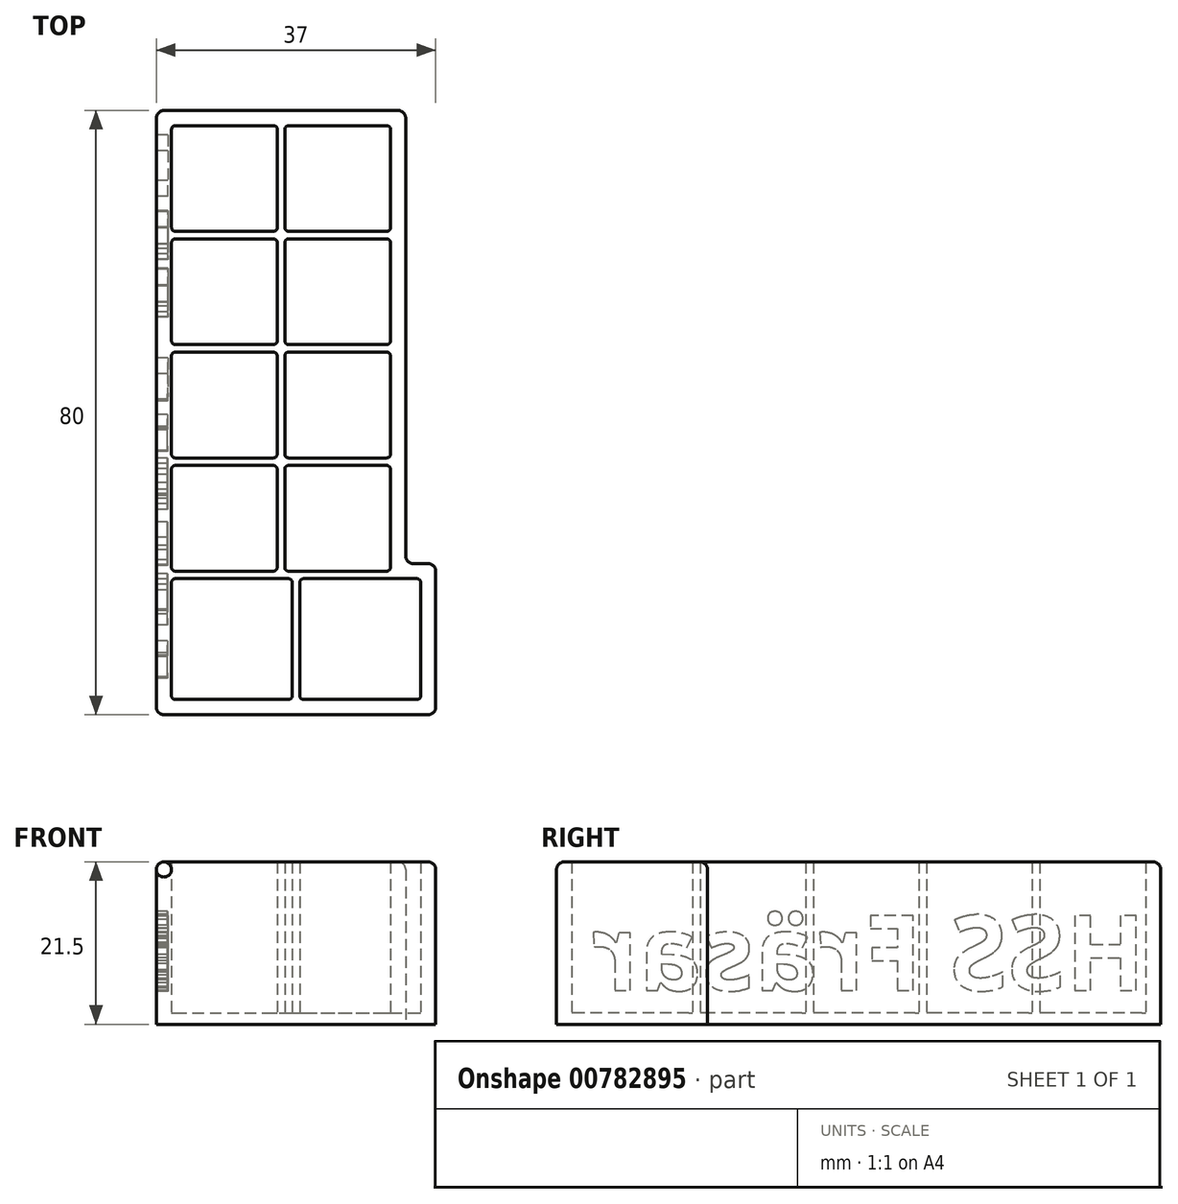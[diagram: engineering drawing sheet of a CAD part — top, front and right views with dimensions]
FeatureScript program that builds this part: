
annotation { "Feature Type Name" : "Feature", "Feature Type Description" : "" }
export const myFeature = defineFeature(function(context is Context, id is Id, definition is map)
    precondition{}
    {
        {
            var Q0;
            Q0=qCreatedBy(makeId("Top.planeOp"),FACE);
            var sketch = newSketch(context, id + "F0", { "sketchPlane" : qUnion([Q0])});
            skLineSegment(sketch, "E0.bottom", {"start": v(-10.2, 14) * mm, "end": v(3.8, 14) * mm});
            skLineSegment(sketch, "E0.top", {"start": v(-10.2, 0) * mm, "end": v(3.8, 0) * mm});
            skLineSegment(sketch, "E0.left", {"start": v(-10.2, 14) * mm, "end": v(-10.2, 0) * mm});
            skLineSegment(sketch, "E0.right", {"start": v(3.8, 14) * mm, "end": v(3.8, 0) * mm});
            skLineSegment(sketch, "E1.0.1.0", {"start": v(-10.2, -1) * mm, "end": v(3.8, -1) * mm});
            skLineSegment(sketch, "E1.0.1.1", {"start": v(-10.2, -1) * mm, "end": v(-10.2, -15) * mm});
            skLineSegment(sketch, "E1.0.1.2", {"start": v(3.8, -1) * mm, "end": v(3.8, -15) * mm});
            skLineSegment(sketch, "E1.0.1.3", {"start": v(-10.2, -15) * mm, "end": v(3.8, -15) * mm});
            skLineSegment(sketch, "E1.0.2.0", {"start": v(-10.2, -16) * mm, "end": v(3.8, -16) * mm});
            skLineSegment(sketch, "E1.0.2.1", {"start": v(-10.2, -16) * mm, "end": v(-10.2, -30) * mm});
            skLineSegment(sketch, "E1.0.2.2", {"start": v(3.8, -16) * mm, "end": v(3.8, -30) * mm});
            skLineSegment(sketch, "E1.0.2.3", {"start": v(-10.2, -30) * mm, "end": v(3.8, -30) * mm});
            skLineSegment(sketch, "E1.0.3.0", {"start": v(-10.2, -31) * mm, "end": v(3.8, -31) * mm});
            skLineSegment(sketch, "E1.0.3.1", {"start": v(-10.2, -31) * mm, "end": v(-10.2, -45) * mm});
            skLineSegment(sketch, "E1.0.3.2", {"start": v(3.8, -31) * mm, "end": v(3.8, -45) * mm});
            skLineSegment(sketch, "E1.0.3.3", {"start": v(-10.2, -45) * mm, "end": v(3.8, -45) * mm});
            skLineSegment(sketch, "E1.1.0.0", {"start": v(4.8, 14) * mm, "end": v(18.8, 14) * mm});
            skLineSegment(sketch, "E1.1.0.1", {"start": v(4.8, 14) * mm, "end": v(4.8, 0) * mm});
            skLineSegment(sketch, "E1.1.0.2", {"start": v(18.8, 14) * mm, "end": v(18.8, 0) * mm});
            skLineSegment(sketch, "E1.1.0.3", {"start": v(4.8, 0) * mm, "end": v(18.8, 0) * mm});
            skLineSegment(sketch, "E1.1.1.0", {"start": v(4.8, -1) * mm, "end": v(18.8, -1) * mm});
            skLineSegment(sketch, "E1.1.1.1", {"start": v(4.8, -1) * mm, "end": v(4.8, -15) * mm});
            skLineSegment(sketch, "E1.1.1.2", {"start": v(18.8, -1) * mm, "end": v(18.8, -15) * mm});
            skLineSegment(sketch, "E1.1.1.3", {"start": v(4.8, -15) * mm, "end": v(18.8, -15) * mm});
            skLineSegment(sketch, "E1.1.2.0", {"start": v(4.8, -16) * mm, "end": v(18.8, -16) * mm});
            skLineSegment(sketch, "E1.1.2.1", {"start": v(4.8, -16) * mm, "end": v(4.8, -30) * mm});
            skLineSegment(sketch, "E1.1.2.2", {"start": v(18.8, -16) * mm, "end": v(18.8, -30) * mm});
            skLineSegment(sketch, "E1.1.2.3", {"start": v(4.8, -30) * mm, "end": v(18.8, -30) * mm});
            skLineSegment(sketch, "E1.1.3.0", {"start": v(4.8, -31) * mm, "end": v(18.8, -31) * mm});
            skLineSegment(sketch, "E1.1.3.1", {"start": v(4.8, -31) * mm, "end": v(4.8, -45) * mm});
            skLineSegment(sketch, "E1.1.3.2", {"start": v(18.8, -31) * mm, "end": v(18.8, -45) * mm});
            skLineSegment(sketch, "E1.1.3.3", {"start": v(4.8, -45) * mm, "end": v(18.8, -45) * mm});
            skLineSegment(sketch, "E1.direction1", {"start": v(-10.2, 14) * mm, "end": v(4.8, 14) * mm, "construction": true});
            skLineSegment(sketch, "E1.direction2", {"start": v(-10.2, 14) * mm, "end": v(-10.2, -1) * mm, "construction": true});
            skLineSegment(sketch, "E2.bottom", {"start": v(-10.2, -46) * mm, "end": v(5.8, -46) * mm});
            skLineSegment(sketch, "E2.top", {"start": v(-10.2, -62) * mm, "end": v(5.8, -62) * mm});
            skLineSegment(sketch, "E2.left", {"start": v(-10.2, -46) * mm, "end": v(-10.2, -62) * mm});
            skLineSegment(sketch, "E2.right", {"start": v(5.8, -46) * mm, "end": v(5.8, -62) * mm});
            skLineSegment(sketch, "E3.1.0.0", {"start": v(22.8, -46) * mm, "end": v(22.8, -62) * mm});
            skLineSegment(sketch, "E3.1.0.1", {"start": v(6.8, -46) * mm, "end": v(22.8, -46) * mm});
            skLineSegment(sketch, "E3.1.0.2", {"start": v(6.8, -46) * mm, "end": v(6.8, -62) * mm});
            skLineSegment(sketch, "E3.1.0.3", {"start": v(6.8, -62) * mm, "end": v(22.8, -62) * mm});
            skLineSegment(sketch, "E3.direction1", {"start": v(5.8, -62) * mm, "end": v(22.8, -62) * mm, "construction": true});
            skSolve(sketch);
        }
        {
            var Q0;
            Q0=qCreatedBy(makeId("Top.planeOp"),FACE);
            var sketch = newSketch(context, id + "F1", { "sketchPlane" : qUnion([Q0])});
            skLineSegment(sketch, "E4", {"start": v(-10.2, 14) * mm, "end": v(18.8, 14) * mm});
            skLineSegment(sketch, "E5", {"start": v(18.8, 14) * mm, "end": v(18.8, -46) * mm});
            skLineSegment(sketch, "E6", {"start": v(18.8, -46) * mm, "end": v(22.8, -46) * mm});
            skLineSegment(sketch, "E7", {"start": v(22.8, -46) * mm, "end": v(22.8, -62) * mm});
            skLineSegment(sketch, "E8", {"start": v(22.8, -62) * mm, "end": v(-10.2, -62) * mm});
            skLineSegment(sketch, "E9", {"start": v(-10.2, -62) * mm, "end": v(-10.2, 14) * mm});
            skLineSegment(sketch, "E10.0", {"start": v(20.8, 16) * mm, "end": v(20.8, -44) * mm});
            skLineSegment(sketch, "E10.1", {"start": v(24.8, -44) * mm, "end": v(24.8, -64) * mm});
            skLineSegment(sketch, "E10.2", {"start": v(24.8, -64) * mm, "end": v(-12.21, -64) * mm});
            skLineSegment(sketch, "E10.3", {"start": v(20.8, -44) * mm, "end": v(24.8, -44) * mm});
            skLineSegment(sketch, "E10.4", {"start": v(-12.21, -64) * mm, "end": v(-12.2, 16) * mm});
            skLineSegment(sketch, "E10.5", {"start": v(-12.2, 16) * mm, "end": v(20.8, 16) * mm});
            skSolve(sketch);
        }
        {
            var Q0;
            Q0=makeQuery(id+"F1.imprint","IMPRINT",FACE,{"disambiguationData":[TD([[makeQuery(id+"F1.imprint","IMPRINT",EDGE,{"derivedFrom":sQuery(id+"F1.wireOp",EDGE,"E4")}),1.0]])]});
            var Q1;
            Q1=makeQuery(id+"F1.imprint","IMPRINT",FACE,{"disambiguationData":[TD([[makeQuery(id+"F1.imprint","IMPRINT",EDGE,{"derivedFrom":sQuery(id+"F1.wireOp",EDGE,"E4")}),-1.0]])]});
            extrude(context, id + "F2", {"entities" : qUnion([Q0, Q1]), "depth" : 20 * mm, "offsetDistance" : 25 * mm, "hasSecondDirection" : true, "secondDirectionOppositeDirection" : true, "secondDirectionDepth" : 1.5 * mm});
        }
        {
            var Q0;
            Q0=makeQuery(id+"F0.imprint","IMPRINT",FACE,{"disambiguationData":[TD([[makeQuery(id+"F0.imprint","IMPRINT",EDGE,{"derivedFrom":sQuery(id+"F0.wireOp",EDGE,"E0.bottom")}),-1.0]])]});
            var Q1;
            Q1=makeQuery(id+"F0.imprint","IMPRINT",FACE,{"disambiguationData":[TD([[makeQuery(id+"F0.imprint","IMPRINT",EDGE,{"derivedFrom":sQuery(id+"F0.wireOp",EDGE,"E1.1.0.0")}),-1.0]])]});
            var Q2;
            Q2=makeQuery(id+"F0.imprint","IMPRINT",FACE,{"disambiguationData":[TD([[makeQuery(id+"F0.imprint","IMPRINT",EDGE,{"derivedFrom":sQuery(id+"F0.wireOp",EDGE,"E1.0.1.0")}),-1.0]])]});
            var Q3;
            Q3=makeQuery(id+"F0.imprint","IMPRINT",FACE,{"disambiguationData":[TD([[makeQuery(id+"F0.imprint","IMPRINT",EDGE,{"derivedFrom":sQuery(id+"F0.wireOp",EDGE,"E1.1.1.0")}),-1.0]])]});
            var Q4;
            Q4=makeQuery(id+"F0.imprint","IMPRINT",FACE,{"disambiguationData":[TD([[makeQuery(id+"F0.imprint","IMPRINT",EDGE,{"derivedFrom":sQuery(id+"F0.wireOp",EDGE,"E1.0.2.0")}),-1.0]])]});
            var Q5;
            Q5=makeQuery(id+"F0.imprint","IMPRINT",FACE,{"disambiguationData":[TD([[makeQuery(id+"F0.imprint","IMPRINT",EDGE,{"derivedFrom":sQuery(id+"F0.wireOp",EDGE,"E1.1.2.0")}),-1.0]])]});
            var Q6;
            Q6=makeQuery(id+"F0.imprint","IMPRINT",FACE,{"disambiguationData":[TD([[makeQuery(id+"F0.imprint","IMPRINT",EDGE,{"derivedFrom":sQuery(id+"F0.wireOp",EDGE,"E1.0.3.0")}),-1.0]])]});
            var Q7;
            Q7=makeQuery(id+"F0.imprint","IMPRINT",FACE,{"disambiguationData":[TD([[makeQuery(id+"F0.imprint","IMPRINT",EDGE,{"derivedFrom":sQuery(id+"F0.wireOp",EDGE,"E1.1.3.0")}),-1.0]])]});
            var Q8;
            Q8=makeQuery(id+"F0.imprint","IMPRINT",FACE,{"disambiguationData":[TD([[makeQuery(id+"F0.imprint","IMPRINT",EDGE,{"derivedFrom":sQuery(id+"F0.wireOp",EDGE,"E2.bottom")}),-1.0]])]});
            var Q9;
            Q9=makeQuery(id+"F0.imprint","IMPRINT",FACE,{"disambiguationData":[TD([[makeQuery(id+"F0.imprint","IMPRINT",EDGE,{"derivedFrom":sQuery(id+"F0.wireOp",EDGE,"E3.1.0.0")}),-1.0]])]});
            var Q10;
            Q10=makeQuery(id+"F2.opExtrude","CAP_FACE",FACE,{"disambiguationData":[OSD([sQuery(id+"F1.wireOp",EDGE,"E10.0"),sQuery(id+"F1.wireOp",EDGE,"E10.1"),sQuery(id+"F1.wireOp",EDGE,"E10.2"),sQuery(id+"F1.wireOp",EDGE,"E10.3"),sQuery(id+"F1.wireOp",EDGE,"E10.4"),sQuery(id+"F1.wireOp",EDGE,"E10.5")])],"isStart":false});
            extrude(context, id + "F3", {"entities" : qUnion([Q0, Q1, Q2, Q3, Q4, Q5, Q6, Q7, Q8, Q9]), "operationType" : NewBodyOperationType.REMOVE, "endBound" : BoundingType.UP_TO_SURFACE, "depth" : 25 * mm, "endBoundEntityFace" : qUnion([Q10]), "offsetDistance" : 25 * mm});
        }
        {
            var Q0;
            Q0=makeQuery(id+"F2.opExtrude","CAP_EDGE",EDGE,{"disambiguationData":[OSD([sQuery(id+"F1.wireOp",EDGE,"E10.0")])],"isStart":false});
            var Q1;
            Q1=makeQuery(id+"F2.opExtrude","CAP_EDGE",EDGE,{"disambiguationData":[OSD([sQuery(id+"F1.wireOp",EDGE,"E10.3")])],"isStart":false});
            var Q2;
            Q2=makeQuery(id+"F2.opExtrude","CAP_EDGE",EDGE,{"disambiguationData":[OSD([sQuery(id+"F1.wireOp",EDGE,"E10.1")])],"isStart":false});
            var Q3;
            Q3=makeQuery(id+"F2.opExtrude","CAP_EDGE",EDGE,{"disambiguationData":[OSD([sQuery(id+"F1.wireOp",EDGE,"E10.4")])],"isStart":false});
            var Q4;
            Q4=makeQuery(id+"F2.opExtrude","SWEPT_EDGE",EDGE,{"disambiguationData":[OSD([sQuery(id+"F1.wireOp",EDGE,"E10.1"),sQuery(id+"F1.wireOp",EDGE,"E10.2")])]});
            var Q5;
            Q5=makeQuery(id+"F2.opExtrude","SWEPT_EDGE",EDGE,{"disambiguationData":[OSD([sQuery(id+"F1.wireOp",EDGE,"E10.1"),sQuery(id+"F1.wireOp",EDGE,"E10.3")])]});
            var Q6;
            Q6=makeQuery(id+"F2.opExtrude","SWEPT_EDGE",EDGE,{"disambiguationData":[OSD([sQuery(id+"F1.wireOp",EDGE,"E10.0"),sQuery(id+"F1.wireOp",EDGE,"E10.5")])]});
            var Q7;
            Q7=makeQuery(id+"F2.opExtrude","CAP_EDGE",EDGE,{"disambiguationData":[OSD([sQuery(id+"F1.wireOp",EDGE,"E10.5")])],"isStart":false});
            var Q8;
            Q8=makeQuery(id+"F2.opExtrude","SWEPT_EDGE",EDGE,{"disambiguationData":[OSD([sQuery(id+"F1.wireOp",EDGE,"E10.4"),sQuery(id+"F1.wireOp",EDGE,"E10.5")])]});
            var Q9;
            Q9=makeQuery(id+"F2.opExtrude","SWEPT_EDGE",EDGE,{"disambiguationData":[OSD([sQuery(id+"F1.wireOp",EDGE,"E10.0"),sQuery(id+"F1.wireOp",EDGE,"E10.3")])]});
            var Q10;
            Q10=makeQuery(id+"F2.opExtrude","CAP_EDGE",EDGE,{"disambiguationData":[OSD([sQuery(id+"F1.wireOp",EDGE,"E10.2")])],"isStart":false});
            var Q11;
            Q11=makeQuery(id+"F2.opExtrude","SWEPT_EDGE",EDGE,{"disambiguationData":[OSD([sQuery(id+"F1.wireOp",EDGE,"E10.2"),sQuery(id+"F1.wireOp",EDGE,"E10.4")])]});
            fillet(context, id + "F4", {"entities" : qUnion([Q0, Q1, Q2, Q3, Q4, Q5, Q6, Q7, Q8, Q9, Q10, Q11]), "radius" : 1 * mm, "allowEdgeOverflow" : false});
        }
        {
            var Q0;
            Q0=makeQuery(id+"F3.boolean.opBoolean","COPY",EDGE,{"derivedFrom":makeQuery(id+"F3.opExtrude","SWEPT_EDGE",EDGE,{"disambiguationData":[OSD([sQuery(id+"F0.wireOp",EDGE,"E1.1.0.0"),sQuery(id+"F0.wireOp",EDGE,"E1.1.0.2")])]})});
            var Q1;
            Q1=makeQuery(id+"F3.boolean.opBoolean","COPY",EDGE,{"derivedFrom":makeQuery(id+"F3.opExtrude","SWEPT_EDGE",EDGE,{"disambiguationData":[OSD([sQuery(id+"F0.wireOp",EDGE,"E1.1.1.0"),sQuery(id+"F0.wireOp",EDGE,"E1.1.1.2")])]})});
            var Q2;
            Q2=makeQuery(id+"F3.boolean.opBoolean","COPY",EDGE,{"derivedFrom":makeQuery(id+"F3.opExtrude","SWEPT_EDGE",EDGE,{"disambiguationData":[OSD([sQuery(id+"F0.wireOp",EDGE,"E1.1.2.0"),sQuery(id+"F0.wireOp",EDGE,"E1.1.2.2")])]})});
            var Q3;
            Q3=makeQuery(id+"F3.boolean.opBoolean","COPY",EDGE,{"derivedFrom":makeQuery(id+"F3.opExtrude","SWEPT_EDGE",EDGE,{"disambiguationData":[OSD([sQuery(id+"F0.wireOp",EDGE,"E1.1.3.0"),sQuery(id+"F0.wireOp",EDGE,"E1.1.3.2")])]})});
            var Q4;
            Q4=makeQuery(id+"F3.boolean.opBoolean","COPY",EDGE,{"derivedFrom":makeQuery(id+"F3.opExtrude","SWEPT_EDGE",EDGE,{"disambiguationData":[OSD([sQuery(id+"F0.wireOp",EDGE,"E3.1.0.0"),sQuery(id+"F0.wireOp",EDGE,"E3.1.0.1")])]})});
            var Q5;
            Q5=makeQuery(id+"F3.boolean.opBoolean","COPY",EDGE,{"derivedFrom":makeQuery(id+"F3.opExtrude","SWEPT_EDGE",EDGE,{"disambiguationData":[OSD([sQuery(id+"F0.wireOp",EDGE,"E0.bottom"),sQuery(id+"F0.wireOp",EDGE,"E0.right")])]})});
            var Q6;
            Q6=makeQuery(id+"F3.boolean.opBoolean","COPY",EDGE,{"derivedFrom":makeQuery(id+"F3.opExtrude","SWEPT_EDGE",EDGE,{"disambiguationData":[OSD([sQuery(id+"F0.wireOp",EDGE,"E1.0.1.0"),sQuery(id+"F0.wireOp",EDGE,"E1.0.1.2")])]})});
            var Q7;
            Q7=makeQuery(id+"F3.boolean.opBoolean","COPY",EDGE,{"derivedFrom":makeQuery(id+"F3.opExtrude","SWEPT_EDGE",EDGE,{"disambiguationData":[OSD([sQuery(id+"F0.wireOp",EDGE,"E1.0.2.0"),sQuery(id+"F0.wireOp",EDGE,"E1.0.2.2")])]})});
            var Q8;
            Q8=makeQuery(id+"F3.boolean.opBoolean","COPY",EDGE,{"derivedFrom":makeQuery(id+"F3.opExtrude","SWEPT_EDGE",EDGE,{"disambiguationData":[OSD([sQuery(id+"F0.wireOp",EDGE,"E1.0.3.0"),sQuery(id+"F0.wireOp",EDGE,"E1.0.3.2")])]})});
            var Q9;
            Q9=makeQuery(id+"F3.boolean.opBoolean","COPY",EDGE,{"derivedFrom":makeQuery(id+"F3.opExtrude","SWEPT_EDGE",EDGE,{"disambiguationData":[OSD([sQuery(id+"F0.wireOp",EDGE,"E2.bottom"),sQuery(id+"F0.wireOp",EDGE,"E2.right")])]})});
            var Q10;
            Q10=makeQuery(id+"F3.boolean.opBoolean","COPY",EDGE,{"derivedFrom":makeQuery(id+"F3.opExtrude","SWEPT_EDGE",EDGE,{"disambiguationData":[OSD([sQuery(id+"F0.wireOp",EDGE,"E1.1.0.2"),sQuery(id+"F0.wireOp",EDGE,"E1.1.0.3")])]})});
            var Q11;
            Q11=makeQuery(id+"F3.boolean.opBoolean","COPY",EDGE,{"derivedFrom":makeQuery(id+"F3.opExtrude","SWEPT_EDGE",EDGE,{"disambiguationData":[OSD([sQuery(id+"F0.wireOp",EDGE,"E1.1.1.2"),sQuery(id+"F0.wireOp",EDGE,"E1.1.1.3")])]})});
            var Q12;
            Q12=makeQuery(id+"F3.boolean.opBoolean","COPY",EDGE,{"derivedFrom":makeQuery(id+"F3.opExtrude","SWEPT_EDGE",EDGE,{"disambiguationData":[OSD([sQuery(id+"F0.wireOp",EDGE,"E1.1.2.2"),sQuery(id+"F0.wireOp",EDGE,"E1.1.2.3")])]})});
            var Q13;
            Q13=makeQuery(id+"F3.boolean.opBoolean","COPY",EDGE,{"derivedFrom":makeQuery(id+"F3.opExtrude","SWEPT_EDGE",EDGE,{"disambiguationData":[OSD([sQuery(id+"F0.wireOp",EDGE,"E1.1.3.2"),sQuery(id+"F0.wireOp",EDGE,"E1.1.3.3")])]})});
            var Q14;
            Q14=makeQuery(id+"F3.boolean.opBoolean","COPY",EDGE,{"derivedFrom":makeQuery(id+"F3.opExtrude","SWEPT_EDGE",EDGE,{"disambiguationData":[OSD([sQuery(id+"F0.wireOp",EDGE,"E3.1.0.0"),sQuery(id+"F0.wireOp",EDGE,"E3.1.0.3")])]})});
            var Q15;
            Q15=makeQuery(id+"F3.boolean.opBoolean","COPY",EDGE,{"derivedFrom":makeQuery(id+"F3.opExtrude","SWEPT_EDGE",EDGE,{"disambiguationData":[OSD([sQuery(id+"F0.wireOp",EDGE,"E2.top"),sQuery(id+"F0.wireOp",EDGE,"E2.right")])]})});
            var Q16;
            Q16=makeQuery(id+"F3.boolean.opBoolean","COPY",EDGE,{"derivedFrom":makeQuery(id+"F3.opExtrude","SWEPT_EDGE",EDGE,{"disambiguationData":[OSD([sQuery(id+"F0.wireOp",EDGE,"E1.0.3.2"),sQuery(id+"F0.wireOp",EDGE,"E1.0.3.3")])]})});
            var Q17;
            Q17=makeQuery(id+"F3.boolean.opBoolean","COPY",EDGE,{"derivedFrom":makeQuery(id+"F3.opExtrude","SWEPT_EDGE",EDGE,{"disambiguationData":[OSD([sQuery(id+"F0.wireOp",EDGE,"E1.0.2.2"),sQuery(id+"F0.wireOp",EDGE,"E1.0.2.3")])]})});
            var Q18;
            Q18=makeQuery(id+"F3.boolean.opBoolean","COPY",EDGE,{"derivedFrom":makeQuery(id+"F3.opExtrude","SWEPT_EDGE",EDGE,{"disambiguationData":[OSD([sQuery(id+"F0.wireOp",EDGE,"E1.0.1.2"),sQuery(id+"F0.wireOp",EDGE,"E1.0.1.3")])]})});
            var Q19;
            Q19=makeQuery(id+"F3.boolean.opBoolean","COPY",EDGE,{"derivedFrom":makeQuery(id+"F3.opExtrude","SWEPT_EDGE",EDGE,{"disambiguationData":[OSD([sQuery(id+"F0.wireOp",EDGE,"E0.top"),sQuery(id+"F0.wireOp",EDGE,"E0.right")])]})});
            var Q20;
            Q20=makeQuery(id+"F3.boolean.opBoolean","COPY",EDGE,{"derivedFrom":makeQuery(id+"F3.opExtrude","SWEPT_EDGE",EDGE,{"disambiguationData":[OSD([sQuery(id+"F0.wireOp",EDGE,"E0.bottom"),sQuery(id+"F0.wireOp",EDGE,"E0.left")])]})});
            var Q21;
            Q21=makeQuery(id+"F3.boolean.opBoolean","COPY",EDGE,{"derivedFrom":makeQuery(id+"F3.opExtrude","SWEPT_EDGE",EDGE,{"disambiguationData":[OSD([sQuery(id+"F0.wireOp",EDGE,"E1.0.1.0"),sQuery(id+"F0.wireOp",EDGE,"E1.0.1.1")])]})});
            var Q22;
            Q22=makeQuery(id+"F3.boolean.opBoolean","COPY",EDGE,{"derivedFrom":makeQuery(id+"F3.opExtrude","SWEPT_EDGE",EDGE,{"disambiguationData":[OSD([sQuery(id+"F0.wireOp",EDGE,"E1.0.2.0"),sQuery(id+"F0.wireOp",EDGE,"E1.0.2.1")])]})});
            var Q23;
            Q23=makeQuery(id+"F3.boolean.opBoolean","COPY",EDGE,{"derivedFrom":makeQuery(id+"F3.opExtrude","SWEPT_EDGE",EDGE,{"disambiguationData":[OSD([sQuery(id+"F0.wireOp",EDGE,"E1.0.3.0"),sQuery(id+"F0.wireOp",EDGE,"E1.0.3.1")])]})});
            var Q24;
            Q24=makeQuery(id+"F3.boolean.opBoolean","COPY",EDGE,{"derivedFrom":makeQuery(id+"F3.opExtrude","SWEPT_EDGE",EDGE,{"disambiguationData":[OSD([sQuery(id+"F0.wireOp",EDGE,"E2.bottom"),sQuery(id+"F0.wireOp",EDGE,"E2.left")])]})});
            var Q25;
            Q25=makeQuery(id+"F3.boolean.opBoolean","COPY",EDGE,{"derivedFrom":makeQuery(id+"F3.opExtrude","SWEPT_EDGE",EDGE,{"disambiguationData":[OSD([sQuery(id+"F0.wireOp",EDGE,"E2.top"),sQuery(id+"F0.wireOp",EDGE,"E2.left")])]})});
            var Q26;
            Q26=makeQuery(id+"F3.boolean.opBoolean","COPY",EDGE,{"derivedFrom":makeQuery(id+"F3.opExtrude","SWEPT_EDGE",EDGE,{"disambiguationData":[OSD([sQuery(id+"F0.wireOp",EDGE,"E1.0.1.1"),sQuery(id+"F0.wireOp",EDGE,"E1.0.1.3")])]})});
            var Q27;
            Q27=makeQuery(id+"F3.boolean.opBoolean","COPY",EDGE,{"derivedFrom":makeQuery(id+"F3.opExtrude","SWEPT_EDGE",EDGE,{"disambiguationData":[OSD([sQuery(id+"F0.wireOp",EDGE,"E0.top"),sQuery(id+"F0.wireOp",EDGE,"E0.left")])]})});
            var Q28;
            Q28=makeQuery(id+"F3.boolean.opBoolean","COPY",EDGE,{"derivedFrom":makeQuery(id+"F3.opExtrude","SWEPT_EDGE",EDGE,{"disambiguationData":[OSD([sQuery(id+"F0.wireOp",EDGE,"E1.1.0.0"),sQuery(id+"F0.wireOp",EDGE,"E1.1.0.1")])]})});
            var Q29;
            Q29=makeQuery(id+"F3.boolean.opBoolean","COPY",EDGE,{"derivedFrom":makeQuery(id+"F3.opExtrude","SWEPT_EDGE",EDGE,{"disambiguationData":[OSD([sQuery(id+"F0.wireOp",EDGE,"E1.1.0.1"),sQuery(id+"F0.wireOp",EDGE,"E1.1.0.3")])]})});
            var Q30;
            Q30=makeQuery(id+"F3.boolean.opBoolean","COPY",EDGE,{"derivedFrom":makeQuery(id+"F3.opExtrude","SWEPT_EDGE",EDGE,{"disambiguationData":[OSD([sQuery(id+"F0.wireOp",EDGE,"E1.1.1.0"),sQuery(id+"F0.wireOp",EDGE,"E1.1.1.1")])]})});
            var Q31;
            Q31=makeQuery(id+"F3.boolean.opBoolean","COPY",EDGE,{"derivedFrom":makeQuery(id+"F3.opExtrude","SWEPT_EDGE",EDGE,{"disambiguationData":[OSD([sQuery(id+"F0.wireOp",EDGE,"E1.1.1.1"),sQuery(id+"F0.wireOp",EDGE,"E1.1.1.3")])]})});
            var Q32;
            Q32=makeQuery(id+"F3.boolean.opBoolean","COPY",EDGE,{"derivedFrom":makeQuery(id+"F3.opExtrude","SWEPT_EDGE",EDGE,{"disambiguationData":[OSD([sQuery(id+"F0.wireOp",EDGE,"E1.1.2.0"),sQuery(id+"F0.wireOp",EDGE,"E1.1.2.1")])]})});
            var Q33;
            Q33=makeQuery(id+"F3.boolean.opBoolean","COPY",EDGE,{"derivedFrom":makeQuery(id+"F3.opExtrude","SWEPT_EDGE",EDGE,{"disambiguationData":[OSD([sQuery(id+"F0.wireOp",EDGE,"E1.0.2.1"),sQuery(id+"F0.wireOp",EDGE,"E1.0.2.3")])]})});
            var Q34;
            Q34=makeQuery(id+"F3.boolean.opBoolean","COPY",EDGE,{"derivedFrom":makeQuery(id+"F3.opExtrude","SWEPT_EDGE",EDGE,{"disambiguationData":[OSD([sQuery(id+"F0.wireOp",EDGE,"E1.1.2.1"),sQuery(id+"F0.wireOp",EDGE,"E1.1.2.3")])]})});
            var Q35;
            Q35=makeQuery(id+"F3.boolean.opBoolean","COPY",EDGE,{"derivedFrom":makeQuery(id+"F3.opExtrude","SWEPT_EDGE",EDGE,{"disambiguationData":[OSD([sQuery(id+"F0.wireOp",EDGE,"E1.1.3.0"),sQuery(id+"F0.wireOp",EDGE,"E1.1.3.1")])]})});
            var Q36;
            Q36=makeQuery(id+"F3.boolean.opBoolean","COPY",EDGE,{"derivedFrom":makeQuery(id+"F3.opExtrude","SWEPT_EDGE",EDGE,{"disambiguationData":[OSD([sQuery(id+"F0.wireOp",EDGE,"E1.1.3.1"),sQuery(id+"F0.wireOp",EDGE,"E1.1.3.3")])]})});
            var Q37;
            Q37=makeQuery(id+"F3.boolean.opBoolean","COPY",EDGE,{"derivedFrom":makeQuery(id+"F3.opExtrude","SWEPT_EDGE",EDGE,{"disambiguationData":[OSD([sQuery(id+"F0.wireOp",EDGE,"E1.0.3.1"),sQuery(id+"F0.wireOp",EDGE,"E1.0.3.3")])]})});
            var Q38;
            Q38=makeQuery(id+"F3.boolean.opBoolean","COPY",EDGE,{"derivedFrom":makeQuery(id+"F3.opExtrude","SWEPT_EDGE",EDGE,{"disambiguationData":[OSD([sQuery(id+"F0.wireOp",EDGE,"E3.1.0.1"),sQuery(id+"F0.wireOp",EDGE,"E3.1.0.2")])]})});
            var Q39;
            Q39=makeQuery(id+"F3.boolean.opBoolean","COPY",EDGE,{"derivedFrom":makeQuery(id+"F3.opExtrude","SWEPT_EDGE",EDGE,{"disambiguationData":[OSD([sQuery(id+"F0.wireOp",EDGE,"E3.1.0.2"),sQuery(id+"F0.wireOp",EDGE,"E3.1.0.3")])]})});
            fillet(context, id + "F5", {"entities" : qUnion([Q0, Q1, Q2, Q3, Q4, Q5, Q6, Q7, Q8, Q9, Q10, Q11, Q12, Q13, Q14, Q15, Q16, Q17, Q18, Q19, Q20, Q21, Q22, Q23, Q24, Q25, Q26, Q27, Q28, Q29, Q30, Q31, Q32, Q33, Q34, Q35, Q36, Q37, Q38, Q39]), "radius" : 0.5 * mm, "tangentPropagation" : true, "allowEdgeOverflow" : false});
        }
        {
            var Q0;
            Q0=makeQuery(id+"F2.opExtrude","SWEPT_FACE",FACE,{"disambiguationData":[OSD([sQuery(id+"F1.wireOp",EDGE,"E10.4")])]});
            var sketch = newSketch(context, id + "F6", { "sketchPlane" : qUnion([Q0])});
            skText(sketch, "E11", { "text": "HSS Fräsar", "fontName": "OpenSans-Bold.ttf"});
            const initialGuessF6  = {"E11": [-0.014, 0.003, 1, 0, 0.01]};
            skSetInitialGuess(sketch, initialGuessF6);
            skSolve(sketch);
        }
        {
            var Q0;
            Q0 = qSketchRegion(id + "F6", true);
            extrude(context, id + "F7", {"entities" : qUnion([Q0]), "operationType" : NewBodyOperationType.REMOVE, "oppositeDirection" : true, "depth" : 1.5 * mm, "offsetDistance" : 25 * mm});
        }
    });
